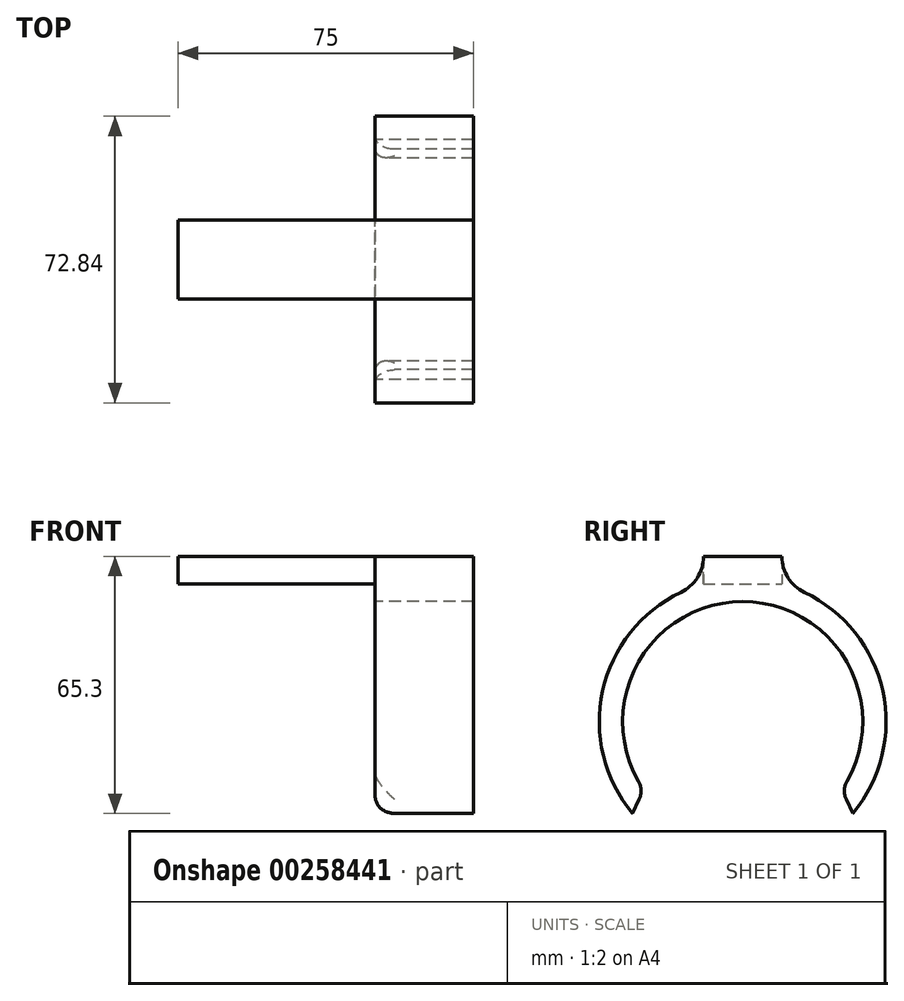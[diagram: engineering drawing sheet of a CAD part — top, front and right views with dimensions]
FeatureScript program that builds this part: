
annotation { "Feature Type Name" : "Feature", "Feature Type Description" : "" }
export const myFeature = defineFeature(function(context is Context, id is Id, definition is map)
    precondition{}
    {
        {
            var Q0;
            Q0=qCreatedBy(makeId("Right.planeOp"),FACE);
            var sketch = newSketch(context, id + "F0", { "sketchPlane" : qUnion([Q0])});
            skArc(sketch, "E0", {"start": v(25.12, -17.3) * mm, "mid": v(0, 30.5) * mm, "end": v(-25.12, -17.3) * mm});
            skArc(sketch, "E1", {"start": v(28, -23.28) * mm, "mid": v(34.8, 10.75) * mm, "end": v(10, 35.02) * mm});
            skLineSegment(sketch, "E2", {"start": v(-28, -23.28) * mm, "end": v(-25.12, -17.3) * mm});
            skLineSegment(sketch, "E3.MirrorCS", {"start": v(28, -23.28) * mm, "end": v(25.12, -17.3) * mm});
            skLineSegment(sketch, "E4", {"start": v(-10, 35.02) * mm, "end": v(10, 35.02) * mm});
            skArc(sketch, "E5.trimOffspring", {"start": v(-10, 35.02) * mm, "mid": v(-34.8, 10.75) * mm, "end": v(-28, -23.28) * mm});
            skSolve(sketch);
        }
        {
            var Q0;
            Q0=makeQuery(id+"F0.imprint","IMPRINT",FACE,{"disambiguationData":[TD([[makeQuery(id+"F0.imprint","IMPRINT",EDGE,{"derivedFrom":sQuery(id+"F0.wireOp",EDGE,"E0")}),-1.0]])]});
            extrude(context, id + "F1", {"entities" : qUnion([Q0]), "depth" : 25 * mm});
        }
        {
            var Q0;
            Q0=makeQuery(id+"F1.opExtrude","SWEPT_FACE",FACE,{"disambiguationData":[OSD([sQuery(id+"F0.wireOp",EDGE,"E4")])]});
            var sketch = newSketch(context, id + "F2", { "sketchPlane" : qUnion([Q0])});
            skLineSegment(sketch, "E6.bottom", {"start": v(-75, 7.5) * mm, "end": v(25, 7.5) * mm});
            skLineSegment(sketch, "E6.top", {"start": v(-75, -7.5) * mm, "end": v(25, -7.5) * mm});
            skLineSegment(sketch, "E6.left", {"start": v(-75, 7.5) * mm, "end": v(-75, -7.5) * mm});
            skPoint(sketch, "E6.middle", {"position": v(25, 0) * mm});
            skLineSegment(sketch, "E7", {"start": v(25, -7.5) * mm, "end": v(25, 7.5) * mm});
            skPoint(sketch, "E6.right.end.orphan", {"position": v(125, -7.5) * mm});
            skPoint(sketch, "E6.right.start.orphan", {"position": v(125, 7.5) * mm});
            skSolve(sketch);
        }
        {
            var Q0;
            {var subQ0=sQuery(id+"F2.wireOp",EDGE,"E6.left");Q0=makeQuery(id+"F2.imprint","IMPRINT",FACE,{"disambiguationData":[TD([[makeQuery(id+"F2.imprint","IMPRINT",EDGE,{"derivedFrom":subQ0}),1.0]])]});}
            var Q1;
            {var subQ0=sQuery(id+"F2.wireOp",EDGE,"E7");Q1=makeQuery(id+"F2.imprint","IMPRINT",FACE,{"disambiguationData":[TD([[makeQuery(id+"F2.imprint","IMPRINT",EDGE,{"derivedFrom":subQ0}),1.0]])]});}
            extrude(context, id + "F3", {"entities" : qUnion([Q0, Q1]), "depth" : 7 * mm});
        }
        {
            var Q0;
            Q0=makeQuery(id+"F1.opExtrude","CAP_EDGE",EDGE,{"disambiguationData":[OSD([sQuery(id+"F0.wireOp",EDGE,"E2")])],"isStart":true});
            var Q1;
            Q1=makeQuery(id+"F1.opExtrude","SWEPT_EDGE",EDGE,{"disambiguationData":[OSD([sQuery(id+"F0.wireOp",EDGE,"E0"),sQuery(id+"F0.wireOp",EDGE,"E3.MirrorCS")])]});
            var Q2;
            Q2=makeQuery(id+"F1.opExtrude","SWEPT_EDGE",EDGE,{"disambiguationData":[OSD([sQuery(id+"F0.wireOp",EDGE,"E0"),sQuery(id+"F0.wireOp",EDGE,"E2")])]});
            var Q3;
            Q3=makeQuery(id+"F1.opExtrude","CAP_EDGE",EDGE,{"disambiguationData":[OSD([sQuery(id+"F0.wireOp",EDGE,"E3.MirrorCS")])],"isStart":true});
            fillet(context, id + "F4", {"entities" : qUnion([Q0, Q1, Q2, Q3]), "radius" : 5 * mm, "tangentPropagation" : true, "allowEdgeOverflow" : false});
        }
        {
            var Q0;
            Q0=makeQuery(id+"F3.opExtrude","SWEPT_BODY",BODY,{"disambiguationData":[OSD([sQuery(id+"F2.wireOp",EDGE,"E6.bottom"),sQuery(id+"F2.wireOp",EDGE,"E6.top"),sQuery(id+"F2.wireOp",EDGE,"E6.left"),sQuery(id+"F2.wireOp",EDGE,"E7")])]});
            deleteBodies(context, id + "F5", {"entities" : qUnion([Q0])});
        }
        {
            var Q0;
            Q0=makeQuery(id+"F1.opExtrude","SWEPT_FACE",FACE,{"disambiguationData":[OSD([sQuery(id+"F0.wireOp",EDGE,"E4")])]});
            var sketch = newSketch(context, id + "F6", { "sketchPlane" : qUnion([Q0])});
            skLineSegment(sketch, "E8.bottom", {"start": v(25, -10) * mm, "end": v(-50, -10) * mm});
            skLineSegment(sketch, "E8.top", {"start": v(25, 10) * mm, "end": v(-50, 10) * mm});
            skLineSegment(sketch, "E8.left", {"start": v(25, -10) * mm, "end": v(25, 10) * mm});
            skLineSegment(sketch, "E8.right", {"start": v(-50, -10) * mm, "end": v(-50, 10) * mm});
            skSolve(sketch);
        }
        {
            var Q0;
            {var subQ2=sQuery(id+"F6.wireOp",EDGE,"E8.right");Q0=makeQuery(id+"F6.imprint","IMPRINT",FACE,{"disambiguationData":[TD([[makeQuery(id+"F6.imprint","IMPRINT",EDGE,{"derivedFrom":subQ2}),-1.0]])]});}
            var Q1;
            {var subQ2=sQuery(id+"F6.wireOp",EDGE,"E8.left");Q1=makeQuery(id+"F6.imprint","IMPRINT",FACE,{"disambiguationData":[TD([[makeQuery(id+"F6.imprint","IMPRINT",EDGE,{"derivedFrom":subQ2}),1.0]])]});}
            extrude(context, id + "F7", {"entities" : qUnion([Q0, Q1]), "operationType" : NewBodyOperationType.ADD, "depth" : 7 * mm});
        }
        {
            var Q0;
            Q0=makeQuery(id+"F7.boolean.opBoolean","MERGE",EDGE,{"derivedFrom":[makeQuery(id+"F1.opExtrude","SWEPT_EDGE",EDGE,{"disambiguationData":[OSD([sQuery(id+"F0.wireOp",EDGE,"E4"),sQuery(id+"F0.wireOp",EDGE,"E5.trimOffspring")])]}),makeQuery(id+"F7.opExtrude","CAP_EDGE",EDGE,{"disambiguationData":[OSD([sQuery(id+"F6.wireOp",EDGE,"E8.bottom")])],"isStart":true})]});
            var Q1;
            Q1=makeQuery(id+"F7.boolean.opBoolean","MERGE",EDGE,{"derivedFrom":[makeQuery(id+"F1.opExtrude","SWEPT_EDGE",EDGE,{"disambiguationData":[OSD([sQuery(id+"F0.wireOp",EDGE,"E1"),sQuery(id+"F0.wireOp",EDGE,"E4")])]}),makeQuery(id+"F7.opExtrude","CAP_EDGE",EDGE,{"disambiguationData":[OSD([sQuery(id+"F6.wireOp",EDGE,"E8.top")])],"isStart":true})]});
            fillet(context, id + "F8", {"entities" : qUnion([Q0, Q1]), "radius" : 10 * mm, "tangentPropagation" : true, "allowEdgeOverflow" : false});
        }
    });
